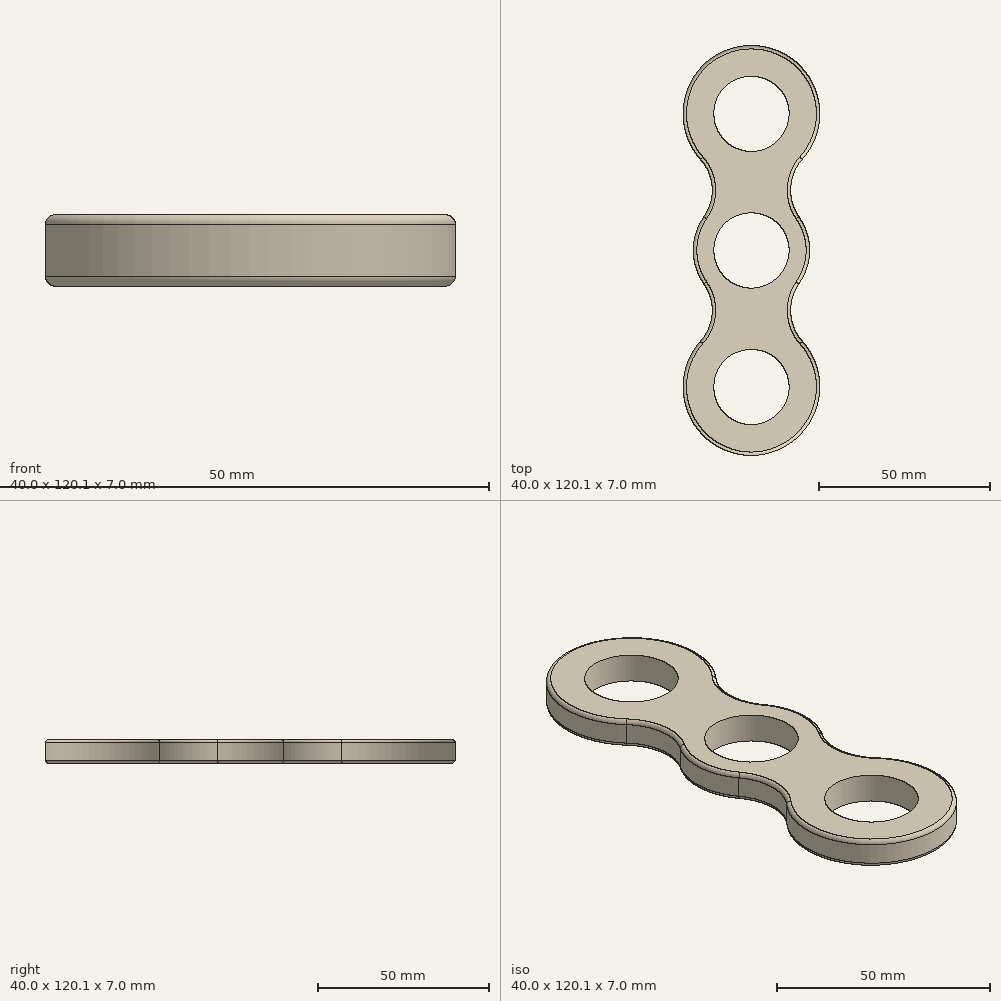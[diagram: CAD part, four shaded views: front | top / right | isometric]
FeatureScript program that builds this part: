
annotation { "Feature Type Name" : "Feature", "Feature Type Description" : "" }
export const myFeature = defineFeature(function(context is Context, id is Id, definition is map)
    precondition{}
    {
        {
            var Q0;
            Q0=qCreatedBy(makeId("Top.planeOp"),FACE);
            var sketch = newSketch(context, id + "F0", { "sketchPlane" : qUnion([Q0])});
            skCircle(sketch, "E0", {"center": v(0, 0) * mm, "radius": 11.03 * mm});
            skCircle(sketch, "E1", {"center": v(0, 40) * mm, "radius": 11.03 * mm});
            skCircle(sketch, "E2.0", {"center": v(0, 40) * mm, "radius": 20.03 * mm});
            skCircle(sketch, "E3.0", {"center": v(0, 0) * mm, "radius": 17.02 * mm});
            skArc(sketch, "E4", {"start": v(-13.94, 9.77) * mm, "mid": v(-11.5, 18.39) * mm, "end": v(-14.94, 26.66) * mm});
            skLineSegment(sketch, "E5", {"start": v(0, -22.67) * mm, "end": v(0, 73.3) * mm, "construction": true});
            skArc(sketch, "E6.MirrorCS", {"start": v(13.94, 9.77) * mm, "mid": v(11.5, 18.39) * mm, "end": v(14.94, 26.66) * mm});
            skArc(sketch, "E7.1.0", {"start": v(13.94, -9.77) * mm, "mid": v(11.5, -18.39) * mm, "end": v(14.94, -26.66) * mm});
            skArc(sketch, "E7.1.1", {"start": v(-13.94, -9.77) * mm, "mid": v(-11.5, -18.39) * mm, "end": v(-14.94, -26.66) * mm});
            skCircle(sketch, "E7.1.2", {"center": v(0, -40) * mm, "radius": 20.03 * mm});
            skCircle(sketch, "E7.1.3", {"center": v(0, -40) * mm, "radius": 11.02 * mm});
            skSolve(sketch);
        }
        {
            var Q0;
            Q0=qSketchRegion(id+"F0",true);
            var Q1;
            Q1=makeQuery(id+"F0.imprint","IMPRINT",FACE,{"disambiguationData":[TD([[makeQuery(id+"F0.imprint","IMPRINT",EDGE,{"derivedFrom":sQuery(id+"F0.wireOp",EDGE,"E0")}),-1.0]])]});
            extrude(context, id + "F1", {"entities" : qUnion([Q0, Q1]), "depth" : 7 * mm, "offsetDistance" : 25 * mm});
        }
        {
            var Q0;
            Q0=makeQuery(id+"F1.opExtrude","SWEPT_FACE",FACE,{"disambiguationData":[OSD([sQuery(id+"F0.wireOp",EDGE,"E2.0")])]});
            var Q1;
            Q1=makeQuery(id+"F1.opExtrude","SWEPT_FACE",FACE,{"disambiguationData":[OSD([sQuery(id+"F0.wireOp",EDGE,"E4")])]});
            var Q2;
            Q2=makeQuery(id+"F1.opExtrude","SWEPT_FACE",FACE,{"disambiguationData":[OSD([sQuery(id+"F0.wireOp",EDGE,"E7.1.1")])]});
            var Q3;
            Q3=makeQuery(id+"F1.opExtrude","SWEPT_FACE",FACE,{"disambiguationData":[OSD([sQuery(id+"F0.wireOp",EDGE,"E7.1.2")])]});
            var Q4;
            Q4=makeQuery(id+"F1.opExtrude","SWEPT_FACE",FACE,{"disambiguationData":[OSD([sQuery(id+"F0.wireOp",EDGE,"E7.2.1")])]});
            fillet(context, id + "F2", {"entities" : qUnion([Q0, Q1, Q2, Q3, Q4]), "radius" : 1 * mm, "tangentPropagation" : true, "allowEdgeOverflow" : false});
        }
    });
